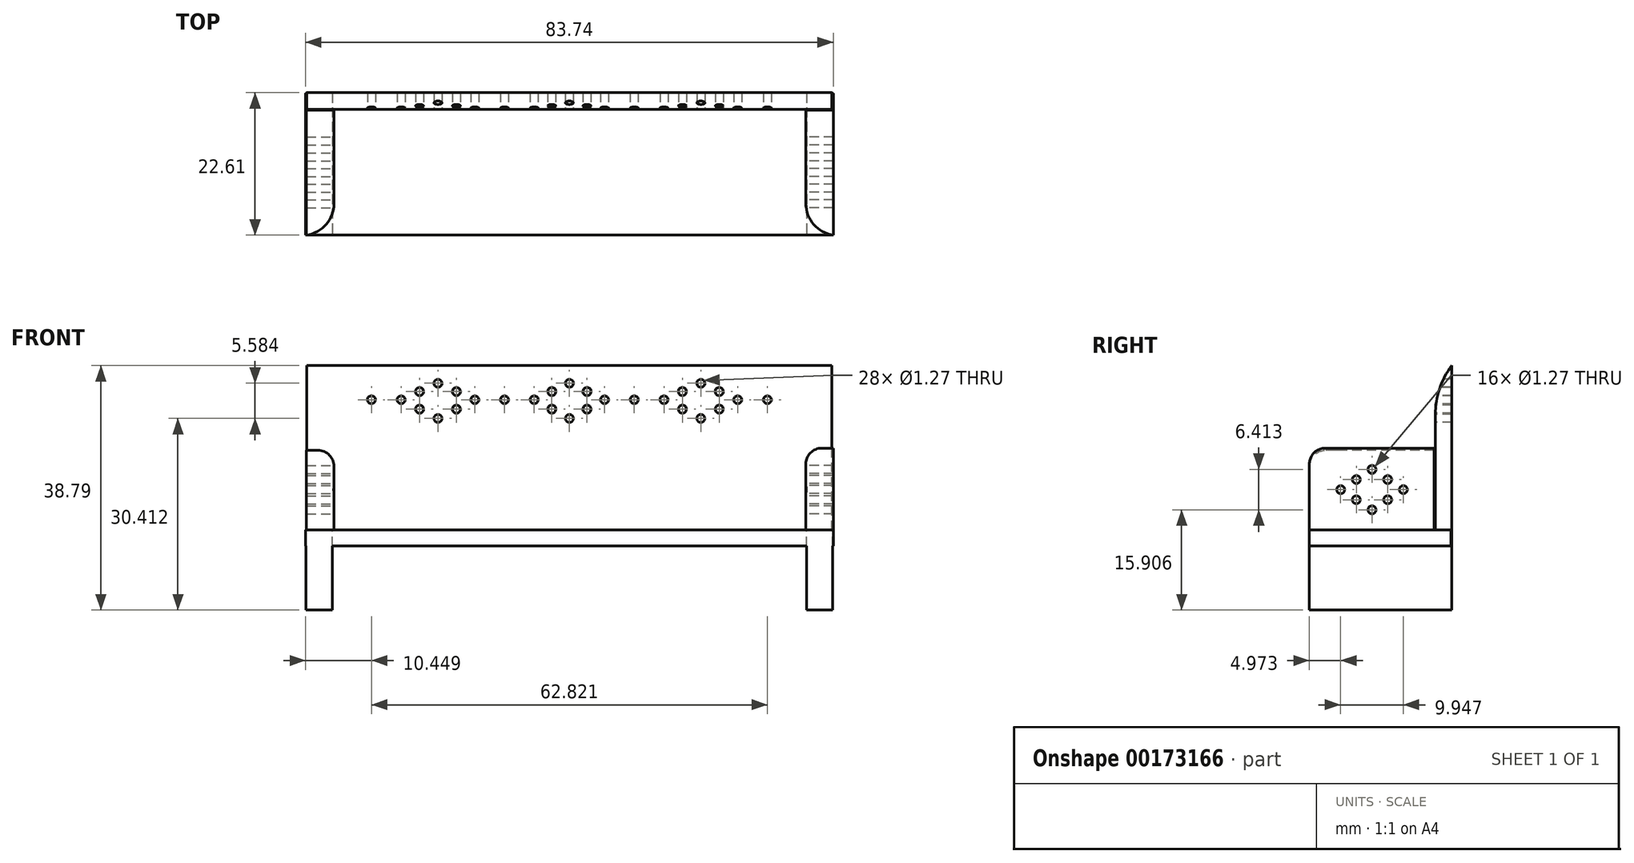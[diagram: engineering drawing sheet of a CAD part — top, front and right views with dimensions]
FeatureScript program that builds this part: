
annotation { "Feature Type Name" : "Feature", "Feature Type Description" : "" }
export const myFeature = defineFeature(function(context is Context, id is Id, definition is map)
    precondition{}
    {
        {
            var Q0;
            Q0=qCreatedBy(makeId("Top.planeOp"),FACE);
            var sketch = newSketch(context, id + "F0", { "sketchPlane" : qUnion([Q0])});
            skLineSegment(sketch, "E0.bottom", {"start": v(0, 0) * mm, "end": v(-41.86, 0) * mm});
            skLineSegment(sketch, "E0.top", {"start": v(0, 22.5) * mm, "end": v(-41.86, 22.5) * mm});
            skLineSegment(sketch, "E0.left", {"start": v(0, 0) * mm, "end": v(0, 22.5) * mm});
            skLineSegment(sketch, "E0.right", {"start": v(-41.86, 0) * mm, "end": v(-41.86, 22.5) * mm});
            skSolve(sketch);
        }
        {
            var Q0;
            Q0=makeQuery(id+"F0.imprint","IMPRINT",FACE,{"disambiguationData":[TD([[makeQuery(id+"F0.imprint","IMPRINT",EDGE,{"derivedFrom":sQuery(id+"F0.wireOp",EDGE,"E0.bottom")}),-1.0]])]});
            extrude(context, id + "F1", {"entities" : qUnion([Q0]), "oppositeDirection" : true, "depth" : 2.54 * mm});
        }
        {
            var Q0;
            Q0=makeQuery(id+"F1.opExtrude","SWEPT_BODY",BODY,{"disambiguationData":[OSD([sQuery(id+"F0.wireOp",EDGE,"E0.bottom"),sQuery(id+"F0.wireOp",EDGE,"E0.top"),sQuery(id+"F0.wireOp",EDGE,"E0.left"),sQuery(id+"F0.wireOp",EDGE,"E0.right")])]});
            var Q1;
            Q1=qCreatedBy(makeId("Right.planeOp"),FACE);
            mirror(context, id + "F2", {"operationType" : NewBodyOperationType.ADD, "entities" : qUnion([Q0]), "mirrorPlane" : qUnion([Q1])});
        }
        {
            var Q0;
            Q0=qCreatedBy(makeId("Top.planeOp"),FACE);
            var sketch = newSketch(context, id + "F3", { "sketchPlane" : qUnion([Q0])});
            skLineSegment(sketch, "E1.bottom", {"start": v(-41.8, 22.59) * mm, "end": v(-37.6, 22.59) * mm});
            skLineSegment(sketch, "E1.top", {"start": v(-41.8, 0) * mm, "end": v(-37.6, 0) * mm});
            skLineSegment(sketch, "E1.left", {"start": v(-41.8, 22.59) * mm, "end": v(-41.8, 0) * mm});
            skLineSegment(sketch, "E1.right", {"start": v(-37.6, 22.59) * mm, "end": v(-37.6, 0) * mm});
            skSolve(sketch);
        }
        {
            var Q0;
            Q0 = qSketchRegion(id + "F3", true);
            extrude(context, id + "F4", {"entities" : qUnion([Q0]), "operationType" : NewBodyOperationType.ADD, "oppositeDirection" : true, "depth" : 12.7 * mm});
        }
        {
            var Q0;
            Q0=makeQuery(id+"F1.opExtrude","SWEPT_BODY",BODY,{"disambiguationData":[OSD([sQuery(id+"F0.wireOp",EDGE,"E0.bottom"),sQuery(id+"F0.wireOp",EDGE,"E0.top"),sQuery(id+"F0.wireOp",EDGE,"E0.left"),sQuery(id+"F0.wireOp",EDGE,"E0.right")])]});
            var Q1;
            Q1=qCreatedBy(makeId("Right.planeOp"),FACE);
            mirror(context, id + "F5", {"operationType" : NewBodyOperationType.ADD, "entities" : qUnion([Q0]), "mirrorPlane" : qUnion([Q1])});
        }
        {
            var Q0;
            Q0=qCreatedBy(makeId("Right.planeOp"),FACE);
            var sketch = newSketch(context, id + "F6", { "sketchPlane" : qUnion([Q0])});
            skLineSegment(sketch, "E2.bottom", {"start": v(22.6, 0) * mm, "end": v(20, 0) * mm});
            skLineSegment(sketch, "E2.top", {"start": v(22.6, 26.09) * mm, "end": v(20, 26.09) * mm});
            skLineSegment(sketch, "E2.left", {"start": v(22.6, 0) * mm, "end": v(22.6, 26.09) * mm});
            skLineSegment(sketch, "E2.right", {"start": v(20, 0) * mm, "end": v(20, 26.09) * mm});
            skSolve(sketch);
        }
        {
            var Q0;
            Q0=makeQuery(id+"F6.imprint","IMPRINT",FACE,{"disambiguationData":[TD([[makeQuery(id+"F6.imprint","IMPRINT",EDGE,{"derivedFrom":sQuery(id+"F6.wireOp",EDGE,"E2.bottom")}),-1.0]])]});
            extrude(context, id + "F7", {"entities" : qUnion([Q0]), "operationType" : NewBodyOperationType.ADD, "depth" : 41.66 * mm});
        }
        {
            var Q0;
            Q0=makeQuery(id+"F1.opExtrude","SWEPT_BODY",BODY,{"disambiguationData":[OSD([sQuery(id+"F0.wireOp",EDGE,"E0.bottom"),sQuery(id+"F0.wireOp",EDGE,"E0.top"),sQuery(id+"F0.wireOp",EDGE,"E0.left"),sQuery(id+"F0.wireOp",EDGE,"E0.right")])]});
            var Q1;
            Q1=qCreatedBy(makeId("Right.planeOp"),FACE);
            mirror(context, id + "F8", {"operationType" : NewBodyOperationType.ADD, "entities" : qUnion([Q0]), "mirrorPlane" : qUnion([Q1])});
        }
        {
            var Q0;
            Q0=qCreatedBy(makeId("Front.planeOp"),FACE);
            var sketch = newSketch(context, id + "F9", { "sketchPlane" : qUnion([Q0])});
            skLineSegment(sketch, "E3.bottom", {"start": v(-41.7, 0) * mm, "end": v(-37.34, 0) * mm});
            skLineSegment(sketch, "E3.top", {"start": v(-41.7, 12.65) * mm, "end": v(-37.34, 12.65) * mm});
            skLineSegment(sketch, "E3.left", {"start": v(-41.7, 0) * mm, "end": v(-41.7, 12.65) * mm});
            skLineSegment(sketch, "E3.right", {"start": v(-37.34, 0) * mm, "end": v(-37.34, 12.65) * mm});
            skSolve(sketch);
        }
        {
            var Q0;
            Q0 = qSketchRegion(id + "F9", true);
            extrude(context, id + "F10", {"entities" : qUnion([Q0]), "operationType" : NewBodyOperationType.ADD, "oppositeDirection" : true, "depth" : 19.8 * mm});
        }
        {
            var Q0;
            Q0=qCreatedBy(makeId("Front.planeOp"),FACE);
            var sketch = newSketch(context, id + "F11", { "sketchPlane" : qUnion([Q0])});
            skLineSegment(sketch, "E4.bottom", {"start": v(41.88, 0) * mm, "end": v(37.52, 0) * mm});
            skLineSegment(sketch, "E4.top", {"start": v(41.88, 13) * mm, "end": v(37.52, 13) * mm});
            skLineSegment(sketch, "E4.left", {"start": v(41.88, 0) * mm, "end": v(41.88, 13) * mm});
            skLineSegment(sketch, "E4.right", {"start": v(37.52, 0) * mm, "end": v(37.52, 13) * mm});
            skSolve(sketch);
        }
        {
            var Q0;
            Q0 = qSketchRegion(id + "F11", true);
            extrude(context, id + "F12", {"entities" : qUnion([Q0]), "operationType" : NewBodyOperationType.ADD, "oppositeDirection" : true, "depth" : 19.8 * mm});
        }
        {
            var Q0;
            {var subQ0=makeQuery(id+"F7.opExtrude","SWEPT_EDGE",EDGE,{"disambiguationData":[OSD([sQuery(id+"F6.wireOp",EDGE,"E2.top"),sQuery(id+"F6.wireOp",EDGE,"E2.right")])]});Q0=makeQuery(id+"F8.boolean.opBoolean","MERGE",EDGE,{"derivedFrom":[subQ0,makeQuery(id+"F8.opPattern","COPY",EDGE,{"derivedFrom":subQ0,"instanceName":"1"})]});}
            fillet(context, id + "F13", {"entities" : qUnion([Q0]), "radius" : 12.88 * mm, "tangentPropagation" : true, "allowEdgeOverflow" : false});
        }
        {
            var Q0;
            Q0=makeQuery(id+"F10.opExtrude","CAP_EDGE",EDGE,{"disambiguationData":[OSD([sQuery(id+"F9.wireOp",EDGE,"E3.right")])],"isStart":true});
            fillet(context, id + "F14", {"entities" : qUnion([Q0]), "radius" : 5.08 * mm, "tangentPropagation" : true, "allowEdgeOverflow" : false});
        }
        {
            var Q0;
            Q0=makeQuery(id+"F12.opExtrude","CAP_EDGE",EDGE,{"disambiguationData":[OSD([sQuery(id+"F11.wireOp",EDGE,"E4.right")])],"isStart":true});
            fillet(context, id + "F15", {"entities" : qUnion([Q0]), "radius" : 5.08 * mm, "tangentPropagation" : true, "allowEdgeOverflow" : false});
        }
        {
            var Q0;
            Q0=makeQuery(id+"F10.opExtrude","SWEPT_EDGE",EDGE,{"disambiguationData":[OSD([sQuery(id+"F9.wireOp",EDGE,"E3.top"),sQuery(id+"F9.wireOp",EDGE,"E3.right")])]});
            fillet(context, id + "F16", {"entities" : qUnion([Q0]), "radius" : 2.54 * mm, "tangentPropagation" : true, "allowEdgeOverflow" : false});
        }
        {
            var Q0;
            Q0=makeQuery(id+"F12.opExtrude","SWEPT_EDGE",EDGE,{"disambiguationData":[OSD([sQuery(id+"F11.wireOp",EDGE,"E4.top"),sQuery(id+"F11.wireOp",EDGE,"E4.right")])]});
            fillet(context, id + "F17", {"entities" : qUnion([Q0]), "radius" : 2.54 * mm, "tangentPropagation" : true, "allowEdgeOverflow" : false});
        }
        {
            var Q0;
            Q0=qCreatedBy(makeId("Front.planeOp"),FACE);
            var sketch = newSketch(context, id + "F18", { "sketchPlane" : qUnion([Q0])});
            skLineSegment(sketch, "E5", {"start": v(41.7, 20.68) * mm, "end": v(-41.7, 20.68) * mm});
            skLineSegment(sketch, "E6", {"start": v(-41.7, 20.68) * mm, "end": v(-41.7, 23.3) * mm});
            skLineSegment(sketch, "E7", {"start": v(-41.7, 23.3) * mm, "end": v(41.53, 23.3) * mm});
            skLineSegment(sketch, "E8", {"start": v(41.53, 23.3) * mm, "end": v(41.7, 20.68) * mm});
            skLineSegment(sketch, "E9", {"start": v(41.7, 17.71) * mm, "end": v(-41.53, 17.71) * mm});
            skLineSegment(sketch, "E10", {"start": v(41.53, 23.3) * mm, "end": v(41.7, 17.71) * mm});
            skLineSegment(sketch, "E11", {"start": v(-41.53, 17.71) * mm, "end": v(-41.7, 23.3) * mm});
            skLineSegment(sketch, "E12", {"start": v(-41.7, 20.68) * mm, "end": v(0, 20.68) * mm});
            skLineSegment(sketch, "E13", {"start": v(0, 20.68) * mm, "end": v(0, 23.3) * mm});
            skLineSegment(sketch, "E14", {"start": v(0, 23.3) * mm, "end": v(0, 17.71) * mm});
            skLineSegment(sketch, "E15", {"start": v(0, 17.71) * mm, "end": v(-41.53, 17.71) * mm});
            skLineSegment(sketch, "E16", {"start": v(0, 20.68) * mm, "end": v(-41.7, 20.68) * mm});
            skPoint(sketch, "E17", {"position": v(-20.85, 20.68) * mm});
            skPoint(sketch, "E18", {"position": v(0, 20.68) * mm});
            skPoint(sketch, "E19", {"position": v(0, 23.3) * mm});
            skPoint(sketch, "E20", {"position": v(0, 17.71) * mm});
            skLineSegment(sketch, "E21", {"start": v(41.7, 20.68) * mm, "end": v(0, 20.68) * mm});
            skPoint(sketch, "E22", {"position": v(20.85, 20.68) * mm});
            skLineSegment(sketch, "E23", {"start": v(0, 20.68) * mm, "end": v(5.58, 20.68) * mm});
            skLineSegment(sketch, "E24", {"start": v(5.58, 20.68) * mm, "end": v(0, 20.68) * mm});
            skLineSegment(sketch, "E25", {"start": v(0, 20.68) * mm, "end": v(-5.58, 20.68) * mm});
            skPoint(sketch, "E26", {"position": v(5.58, 20.68) * mm});
            skPoint(sketch, "E27", {"position": v(-5.58, 20.68) * mm});
            skLineSegment(sketch, "E28", {"start": v(5.58, 20.68) * mm, "end": v(0, 23.3) * mm});
            skLineSegment(sketch, "E29", {"start": v(-5.58, 20.68) * mm, "end": v(0, 23.3) * mm});
            skLineSegment(sketch, "E30", {"start": v(-5.58, 20.68) * mm, "end": v(0, 17.71) * mm});
            skLineSegment(sketch, "E31", {"start": v(5.58, 20.68) * mm, "end": v(0, 17.71) * mm});
            skPoint(sketch, "E32", {"position": v(-2.8, 19.2) * mm});
            skPoint(sketch, "E33", {"position": v(-2.8, 21.99) * mm});
            skPoint(sketch, "E34", {"position": v(2.8, 21.99) * mm});
            skPoint(sketch, "E35", {"position": v(2.8, 19.2) * mm});
            skLineSegment(sketch, "E36", {"start": v(20.85, 20.68) * mm, "end": v(20.85, 23.3) * mm});
            skLineSegment(sketch, "E37", {"start": v(20.85, 23.3) * mm, "end": v(20.85, 20.68) * mm});
            skLineSegment(sketch, "E38", {"start": v(20.85, 17.71) * mm, "end": v(20.85, 20.68) * mm});
            skPoint(sketch, "E39", {"position": v(20.85, 23.3) * mm});
            skPoint(sketch, "E40", {"position": v(20.85, 17.71) * mm});
            skLineSegment(sketch, "E41", {"start": v(20.85, 20.68) * mm, "end": v(15, 20.68) * mm});
            skLineSegment(sketch, "E42", {"start": v(15, 20.68) * mm, "end": v(20.85, 20.68) * mm});
            skLineSegment(sketch, "E43", {"start": v(20.85, 20.68) * mm, "end": v(26.7, 20.68) * mm});
            skLineSegment(sketch, "E44", {"start": v(26.7, 20.68) * mm, "end": v(20.85, 23.3) * mm});
            skLineSegment(sketch, "E45", {"start": v(20.85, 23.3) * mm, "end": v(15, 20.68) * mm});
            skLineSegment(sketch, "E46", {"start": v(15, 20.68) * mm, "end": v(20.85, 17.71) * mm});
            skLineSegment(sketch, "E47", {"start": v(20.85, 17.71) * mm, "end": v(26.7, 20.68) * mm});
            skPoint(sketch, "E48", {"position": v(26.7, 20.68) * mm});
            skPoint(sketch, "E49", {"position": v(15, 20.68) * mm});
            skPoint(sketch, "E50", {"position": v(17.93, 19.2) * mm});
            skPoint(sketch, "E51", {"position": v(17.93, 21.99) * mm});
            skPoint(sketch, "E52", {"position": v(23.78, 21.99) * mm});
            skPoint(sketch, "E53", {"position": v(23.78, 19.2) * mm});
            skLineSegment(sketch, "E54", {"start": v(-20.85, 20.68) * mm, "end": v(-20.85, 23.3) * mm});
            skLineSegment(sketch, "E55", {"start": v(-20.85, 23.3) * mm, "end": v(-20.85, 20.68) * mm});
            skLineSegment(sketch, "E56", {"start": v(-20.85, 17.71) * mm, "end": v(-20.85, 20.68) * mm});
            skLineSegment(sketch, "E57", {"start": v(-20.85, 20.68) * mm, "end": v(-26.7, 20.68) * mm});
            skLineSegment(sketch, "E58", {"start": v(-26.7, 20.68) * mm, "end": v(-20.85, 20.68) * mm});
            skLineSegment(sketch, "E59", {"start": v(-20.85, 20.68) * mm, "end": v(-15, 20.68) * mm});
            skLineSegment(sketch, "E60", {"start": v(-20.85, 23.3) * mm, "end": v(-15, 20.68) * mm});
            skLineSegment(sketch, "E61", {"start": v(-20.85, 17.71) * mm, "end": v(-15, 20.68) * mm});
            skLineSegment(sketch, "E62", {"start": v(-20.85, 17.71) * mm, "end": v(-26.7, 20.68) * mm});
            skLineSegment(sketch, "E63", {"start": v(-26.7, 20.68) * mm, "end": v(-20.85, 23.3) * mm});
            skPoint(sketch, "E64", {"position": v(-20.85, 23.3) * mm});
            skPoint(sketch, "E65", {"position": v(-26.7, 20.68) * mm});
            skPoint(sketch, "E66", {"position": v(-20.85, 17.71) * mm});
            skPoint(sketch, "E67", {"position": v(-15, 20.68) * mm});
            skPoint(sketch, "E68", {"position": v(-17.93, 19.2) * mm});
            skPoint(sketch, "E69", {"position": v(-23.78, 19.2) * mm});
            skPoint(sketch, "E70", {"position": v(-23.78, 21.99) * mm});
            skPoint(sketch, "E71", {"position": v(-17.93, 21.99) * mm});
            skLineSegment(sketch, "E72", {"start": v(15, 20.68) * mm, "end": v(5.58, 20.68) * mm});
            skLineSegment(sketch, "E73", {"start": v(-5.58, 20.68) * mm, "end": v(-15, 20.68) * mm});
            skPoint(sketch, "E74", {"position": v(10.3, 20.68) * mm});
            skPoint(sketch, "E75", {"position": v(-10.3, 20.68) * mm});
            skLineSegment(sketch, "E76", {"start": v(26.7, 20.68) * mm, "end": v(36.12, 20.68) * mm});
            skLineSegment(sketch, "E77", {"start": v(36.12, 20.68) * mm, "end": v(26.7, 20.68) * mm});
            skPoint(sketch, "E78", {"position": v(31.41, 20.68) * mm});
            skLineSegment(sketch, "E79", {"start": v(-26.7, 20.68) * mm, "end": v(-36.12, 20.68) * mm});
            skPoint(sketch, "E80", {"position": v(-31.41, 20.68) * mm});
            skSolve(sketch);
        }
        {
            var Q0;
            Q0=sQuery(id+"F18.wireOp",VERTEX,"E78");
            var Q1;
            Q1=sQuery(id+"F18.wireOp",VERTEX,"E48");
            var Q2;
            Q2=sQuery(id+"F18.wireOp",VERTEX,"E52");
            var Q3;
            Q3=sQuery(id+"F18.wireOp",VERTEX,"E39");
            var Q4;
            Q4=sQuery(id+"F18.wireOp",VERTEX,"E51");
            var Q5;
            Q5=sQuery(id+"F18.wireOp",VERTEX,"E49");
            var Q6;
            Q6=sQuery(id+"F18.wireOp",VERTEX,"E50");
            var Q7;
            Q7=sQuery(id+"F18.wireOp",VERTEX,"E40");
            var Q8;
            Q8=sQuery(id+"F18.wireOp",VERTEX,"E53");
            var Q9;
            Q9=sQuery(id+"F18.wireOp",VERTEX,"E74");
            var Q10;
            Q10=sQuery(id+"F18.wireOp",VERTEX,"E26");
            var Q11;
            Q11=sQuery(id+"F18.wireOp",VERTEX,"E34");
            var Q12;
            Q12=sQuery(id+"F18.wireOp",VERTEX,"E19");
            var Q13;
            Q13=sQuery(id+"F18.wireOp",VERTEX,"E33");
            var Q14;
            Q14=sQuery(id+"F18.wireOp",VERTEX,"E27");
            var Q15;
            Q15=sQuery(id+"F18.wireOp",VERTEX,"E32");
            var Q16;
            Q16=sQuery(id+"F18.wireOp",VERTEX,"E35");
            var Q17;
            Q17=sQuery(id+"F18.wireOp",VERTEX,"E20");
            var Q18;
            Q18=sQuery(id+"F18.wireOp",VERTEX,"E75");
            var Q19;
            Q19=sQuery(id+"F18.wireOp",VERTEX,"E67");
            var Q20;
            Q20=sQuery(id+"F18.wireOp",VERTEX,"E71");
            var Q21;
            Q21=sQuery(id+"F18.wireOp",VERTEX,"E64");
            var Q22;
            Q22=sQuery(id+"F18.wireOp",VERTEX,"E70");
            var Q23;
            Q23=sQuery(id+"F18.wireOp",VERTEX,"E65");
            var Q24;
            Q24=sQuery(id+"F18.wireOp",VERTEX,"E69");
            var Q25;
            Q25=sQuery(id+"F18.wireOp",VERTEX,"E66");
            var Q26;
            Q26=sQuery(id+"F18.wireOp",VERTEX,"E68");
            var Q27;
            Q27=sQuery(id+"F18.wireOp",VERTEX,"E80");
            var Q28;
            Q28=makeQuery(id+"F1.opExtrude","SWEPT_BODY",BODY,{"disambiguationData":[OSD([sQuery(id+"F0.wireOp",EDGE,"E0.bottom"),sQuery(id+"F0.wireOp",EDGE,"E0.top"),sQuery(id+"F0.wireOp",EDGE,"E0.left"),sQuery(id+"F0.wireOp",EDGE,"E0.right")])]});
            hole(context, id + "F19", {"style" : HoleStyle.SIMPLE, "endStyle" : HoleEndStyle.THROUGH, "holeDiameter" : 1.27 * mm, "locations" : qUnion([Q0, Q1, Q2, Q3, Q4, Q5, Q6, Q7, Q8, Q9, Q10, Q11, Q12, Q13, Q14, Q15, Q16, Q17, Q18, Q19, Q20, Q21, Q22, Q23, Q24, Q25, Q26, Q27]), "scope" : qUnion([Q28]), "isTappedThrough" : true});
        }
        {
            var Q0;
            Q0=qCreatedBy(makeId("Right.planeOp"),FACE);
            var sketch = newSketch(context, id + "F20", { "sketchPlane" : qUnion([Q0])});
            skLineSegment(sketch, "E81", {"start": v(19.9, 0) * mm, "end": v(0, 0) * mm});
            skLineSegment(sketch, "E82", {"start": v(0, 0) * mm, "end": v(19.9, 0) * mm});
            skLineSegment(sketch, "E83", {"start": v(19.9, 12.83) * mm, "end": v(0, 12.83) * mm});
            skLineSegment(sketch, "E84", {"start": v(0, 12.83) * mm, "end": v(0, 0) * mm});
            skPoint(sketch, "E85", {"position": v(0, 6.41) * mm});
            skLineSegment(sketch, "E86", {"start": v(19.9, 12.83) * mm, "end": v(19.9, 0) * mm});
            skPoint(sketch, "E87", {"position": v(19.9, 6.41) * mm});
            skLineSegment(sketch, "E88", {"start": v(19.9, 6.41) * mm, "end": v(0, 6.41) * mm});
            skPoint(sketch, "E89", {"position": v(9.95, 6.41) * mm});
            skLineSegment(sketch, "E90", {"start": v(9.95, 6.41) * mm, "end": v(9.95, 12.83) * mm});
            skLineSegment(sketch, "E91", {"start": v(9.95, 12.83) * mm, "end": v(9.95, 6.41) * mm});
            skLineSegment(sketch, "E92", {"start": v(9.95, 6.41) * mm, "end": v(9.95, 0) * mm});
            skPoint(sketch, "E93", {"position": v(9.95, 9.62) * mm});
            skPoint(sketch, "E94", {"position": v(9.95, 3.2) * mm});
            skLineSegment(sketch, "E95", {"start": v(19.9, 6.41) * mm, "end": v(9.95, 6.41) * mm});
            skPoint(sketch, "E96", {"position": v(14.92, 6.41) * mm});
            skLineSegment(sketch, "E97", {"start": v(9.95, 6.41) * mm, "end": v(0, 6.41) * mm});
            skPoint(sketch, "E98", {"position": v(4.97, 6.41) * mm});
            skLineSegment(sketch, "E99", {"start": v(14.92, 6.41) * mm, "end": v(9.95, 9.62) * mm});
            skLineSegment(sketch, "E100", {"start": v(4.97, 6.41) * mm, "end": v(9.95, 9.62) * mm});
            skLineSegment(sketch, "E101", {"start": v(14.92, 6.41) * mm, "end": v(9.95, 3.2) * mm});
            skLineSegment(sketch, "E102", {"start": v(9.95, 3.2) * mm, "end": v(4.97, 6.41) * mm});
            skPoint(sketch, "E103", {"position": v(12.43, 8.02) * mm});
            skPoint(sketch, "E104", {"position": v(7.46, 8.02) * mm});
            skPoint(sketch, "E105", {"position": v(7.46, 4.8) * mm});
            skPoint(sketch, "E106", {"position": v(12.43, 4.8) * mm});
            skSolve(sketch);
        }
        {
            var Q0;
            Q0=sQuery(id+"F20.wireOp",VERTEX,"E96");
            var Q1;
            Q1=sQuery(id+"F20.wireOp",VERTEX,"E103");
            var Q2;
            Q2=sQuery(id+"F20.wireOp",VERTEX,"E93");
            var Q3;
            Q3=sQuery(id+"F20.wireOp",VERTEX,"E104");
            var Q4;
            Q4=sQuery(id+"F20.wireOp",VERTEX,"E98");
            var Q5;
            Q5=sQuery(id+"F20.wireOp",VERTEX,"E106");
            var Q6;
            Q6=sQuery(id+"F20.wireOp",VERTEX,"E94");
            var Q7;
            Q7=sQuery(id+"F20.wireOp",VERTEX,"E105");
            var Q8;
            Q8=makeQuery(id+"F1.opExtrude","SWEPT_BODY",BODY,{"disambiguationData":[OSD([sQuery(id+"F0.wireOp",EDGE,"E0.bottom"),sQuery(id+"F0.wireOp",EDGE,"E0.top"),sQuery(id+"F0.wireOp",EDGE,"E0.left"),sQuery(id+"F0.wireOp",EDGE,"E0.right")])]});
            hole(context, id + "F21", {"style" : HoleStyle.SIMPLE, "endStyle" : HoleEndStyle.THROUGH, "holeDiameter" : 1.27 * mm, "locations" : qUnion([Q0, Q1, Q2, Q3, Q4, Q5, Q6, Q7]), "scope" : qUnion([Q8]), "isTappedThrough" : true});
        }
        {
            var Q0;
            Q0=qCreatedBy(makeId("Right.planeOp"),FACE);
            var sketch = newSketch(context, id + "F22", { "sketchPlane" : qUnion([Q0])});
            skLineSegment(sketch, "E107", {"start": v(0, 0) * mm, "end": v(19.9, 0) * mm});
            skLineSegment(sketch, "E108", {"start": v(19.9, 0) * mm, "end": v(19.9, 12.83) * mm});
            skLineSegment(sketch, "E109", {"start": v(19.9, 12.83) * mm, "end": v(0, 12.83) * mm});
            skLineSegment(sketch, "E110", {"start": v(0, 12.83) * mm, "end": v(0, 0) * mm});
            skLineSegment(sketch, "E111", {"start": v(19.9, 0) * mm, "end": v(19.9, 6.41) * mm});
            skLineSegment(sketch, "E112", {"start": v(19.9, 6.41) * mm, "end": v(0, 6.41) * mm});
            skLineSegment(sketch, "E113", {"start": v(0, 6.41) * mm, "end": v(9.95, 6.41) * mm});
            skLineSegment(sketch, "E114", {"start": v(9.95, 6.41) * mm, "end": v(9.95, 12.83) * mm});
            skLineSegment(sketch, "E115", {"start": v(9.95, 12.83) * mm, "end": v(9.95, 9.62) * mm});
            skLineSegment(sketch, "E116", {"start": v(9.95, 9.62) * mm, "end": v(9.95, 6.41) * mm});
            skLineSegment(sketch, "E117", {"start": v(9.95, 0) * mm, "end": v(9.95, 6.41) * mm});
            skLineSegment(sketch, "E118", {"start": v(9.95, 3.2) * mm, "end": v(9.95, 6.41) * mm});
            skLineSegment(sketch, "E119", {"start": v(19.9, 6.41) * mm, "end": v(9.95, 6.41) * mm});
            skLineSegment(sketch, "E120", {"start": v(14.92, 6.41) * mm, "end": v(9.95, 6.41) * mm});
            skLineSegment(sketch, "E121", {"start": v(9.95, 6.41) * mm, "end": v(0, 6.41) * mm});
            skLineSegment(sketch, "E122", {"start": v(4.97, 6.41) * mm, "end": v(9.95, 9.62) * mm});
            skLineSegment(sketch, "E123", {"start": v(7.46, 8.02) * mm, "end": v(4.97, 6.41) * mm});
            skLineSegment(sketch, "E124", {"start": v(4.97, 6.41) * mm, "end": v(9.95, 3.2) * mm});
            skLineSegment(sketch, "E125", {"start": v(7.46, 4.8) * mm, "end": v(9.95, 3.2) * mm});
            skLineSegment(sketch, "E126", {"start": v(14.92, 6.41) * mm, "end": v(9.95, 3.2) * mm});
            skLineSegment(sketch, "E127", {"start": v(12.43, 4.8) * mm, "end": v(14.92, 6.41) * mm});
            skLineSegment(sketch, "E128", {"start": v(14.92, 6.41) * mm, "end": v(9.95, 9.62) * mm});
            skLineSegment(sketch, "E129", {"start": v(12.43, 8.02) * mm, "end": v(14.92, 6.41) * mm});
            skPoint(sketch, "E130", {"position": v(9.95, 9.62) * mm});
            skPoint(sketch, "E131", {"position": v(7.46, 8.02) * mm});
            skPoint(sketch, "E132", {"position": v(4.97, 6.41) * mm});
            skPoint(sketch, "E133", {"position": v(7.46, 4.8) * mm});
            skPoint(sketch, "E134", {"position": v(9.95, 3.2) * mm});
            skPoint(sketch, "E135", {"position": v(12.43, 4.8) * mm});
            skPoint(sketch, "E136", {"position": v(14.92, 6.41) * mm});
            skPoint(sketch, "E137", {"position": v(12.43, 8.02) * mm});
            skSolve(sketch);
        }
        {
            var Q0;
            Q0=sQuery(id+"F22.wireOp",VERTEX,"E130");
            var Q1;
            Q1=sQuery(id+"F22.wireOp",VERTEX,"E131");
            var Q2;
            Q2=sQuery(id+"F22.wireOp",VERTEX,"E132");
            var Q3;
            Q3=sQuery(id+"F22.wireOp",VERTEX,"E133");
            var Q4;
            Q4=sQuery(id+"F22.wireOp",VERTEX,"E134");
            var Q5;
            Q5=sQuery(id+"F22.wireOp",VERTEX,"E135");
            var Q6;
            Q6=sQuery(id+"F22.wireOp",VERTEX,"E136");
            var Q7;
            Q7=sQuery(id+"F22.wireOp",VERTEX,"E137");
            var Q8;
            Q8=makeQuery(id+"F1.opExtrude","SWEPT_BODY",BODY,{"disambiguationData":[OSD([sQuery(id+"F0.wireOp",EDGE,"E0.bottom"),sQuery(id+"F0.wireOp",EDGE,"E0.top"),sQuery(id+"F0.wireOp",EDGE,"E0.left"),sQuery(id+"F0.wireOp",EDGE,"E0.right")])]});
            hole(context, id + "F23", {"style" : HoleStyle.SIMPLE, "endStyle" : HoleEndStyle.THROUGH, "oppositeDirection" : true, "holeDiameter" : 1.27 * mm, "locations" : qUnion([Q0, Q1, Q2, Q3, Q4, Q5, Q6, Q7]), "scope" : qUnion([Q8]), "isTappedThrough" : true});
        }
    });
